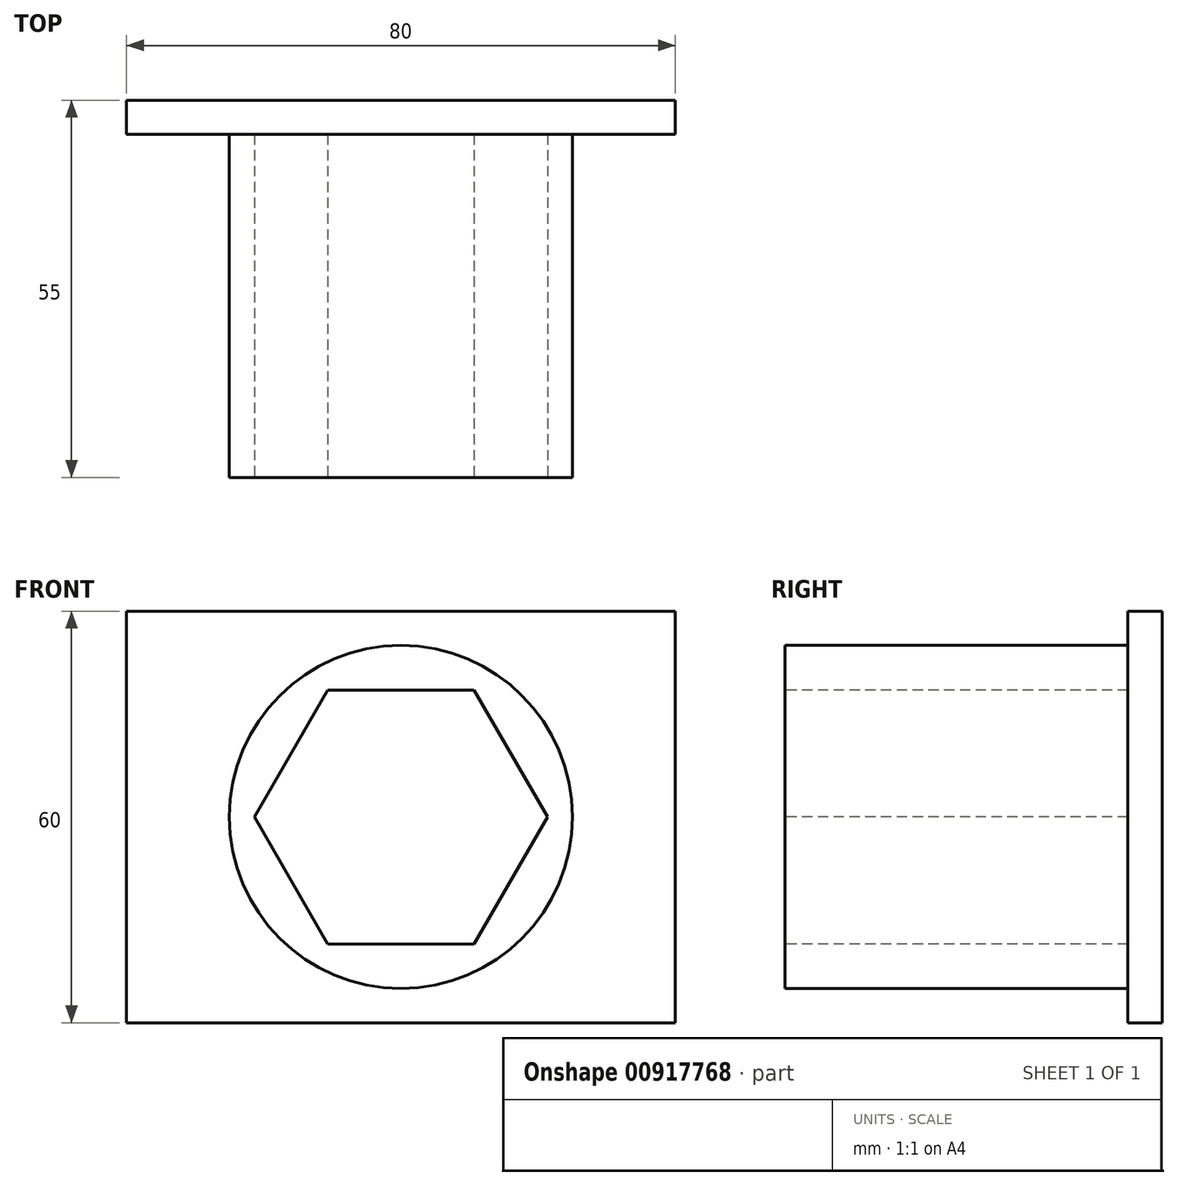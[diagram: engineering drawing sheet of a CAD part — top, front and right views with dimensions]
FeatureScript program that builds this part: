
annotation { "Feature Type Name" : "Feature", "Feature Type Description" : "" }
export const myFeature = defineFeature(function(context is Context, id is Id, definition is map)
    precondition{}
    {
        {
            var Q0;
            Q0=qCreatedBy(makeId("Front.planeOp"),FACE);
            var sketch = newSketch(context, id + "F0", { "sketchPlane" : qUnion([Q0])});
            skLineSegment(sketch, "E0.bottom", {"start": v(40, -30) * mm, "end": v(-40, -30) * mm});
            skLineSegment(sketch, "E0.top", {"start": v(40, 30) * mm, "end": v(-40, 30) * mm});
            skLineSegment(sketch, "E0.left", {"start": v(40, -30) * mm, "end": v(40, 30) * mm});
            skLineSegment(sketch, "E0.right", {"start": v(-40, -30) * mm, "end": v(-40, 30) * mm});
            skPoint(sketch, "E0.middle", {"position": v(0, 0) * mm});
            skSolve(sketch);
        }
        {
            var Q0;
            Q0 = qSketchRegion(id + "F0", true);
            extrude(context, id + "F1", {"entities" : qUnion([Q0]), "depth" : 5 * mm, "offsetDistance" : 25 * mm});
        }
        {
            var Q0;
            Q0=makeQuery(id+"F1.opExtrude","CAP_FACE",FACE,{"disambiguationData":[OSD([sQuery(id+"F0.wireOp",EDGE,"E0.bottom"),sQuery(id+"F0.wireOp",EDGE,"E0.top"),sQuery(id+"F0.wireOp",EDGE,"E0.left"),sQuery(id+"F0.wireOp",EDGE,"E0.right")])],"isStart":false});
            var sketch = newSketch(context, id + "F2", { "sketchPlane" : qUnion([Q0])});
            skCircle(sketch, "E1", {"center": v(0, 0) * mm, "radius": 25 * mm});
            skSolve(sketch);
        }
        {
            var Q0;
            Q0 = qSketchRegion(id + "F2", true);
            extrude(context, id + "F3", {"entities" : qUnion([Q0]), "operationType" : NewBodyOperationType.ADD, "depth" : 50 * mm, "offsetDistance" : 25 * mm});
        }
        {
            var Q0;
            Q0=makeQuery(id+"F3.opExtrude","CAP_FACE",FACE,{"disambiguationData":[OSD([sQuery(id+"F2.wireOp",EDGE,"E1")])],"isStart":false});
            var sketch = newSketch(context, id + "F4", { "sketchPlane" : qUnion([Q0])});
            skCircle(sketch, "E2.cCircle", {"center": v(0, 0) * mm, "radius": 18.5 * mm, "construction": true});
            skLineSegment(sketch, "E2.0", {"start": v(21.36, 0) * mm, "end": v(10.68, -18.5) * mm});
            skLineSegment(sketch, "E2.1", {"start": v(10.68, -18.5) * mm, "end": v(-10.68, -18.5) * mm});
            skLineSegment(sketch, "E2.2", {"start": v(-10.68, -18.5) * mm, "end": v(-21.36, 0) * mm});
            skLineSegment(sketch, "E2.3", {"start": v(-21.36, 0) * mm, "end": v(-10.68, 18.5) * mm});
            skLineSegment(sketch, "E2.4", {"start": v(-10.68, 18.5) * mm, "end": v(10.68, 18.5) * mm});
            skLineSegment(sketch, "E2.5", {"start": v(10.68, 18.5) * mm, "end": v(21.36, 0) * mm});
            skPoint(sketch, "E2.0.midPoint", {"position": v(16.02, -9.25) * mm});
            skSolve(sketch);
        }
        {
            var Q0;
            Q0=makeQuery(id+"F4.imprint","IMPRINT",FACE,{"disambiguationData":[TD([[makeQuery(id+"F4.imprint","IMPRINT",EDGE,{"derivedFrom":sQuery(id+"F4.wireOp",EDGE,"E2.0")}),-1.0]])]});
            extrude(context, id + "F5", {"entities" : qUnion([Q0]), "operationType" : NewBodyOperationType.REMOVE, "oppositeDirection" : true, "depth" : 50 * mm, "offsetDistance" : 25 * mm});
        }
    });
